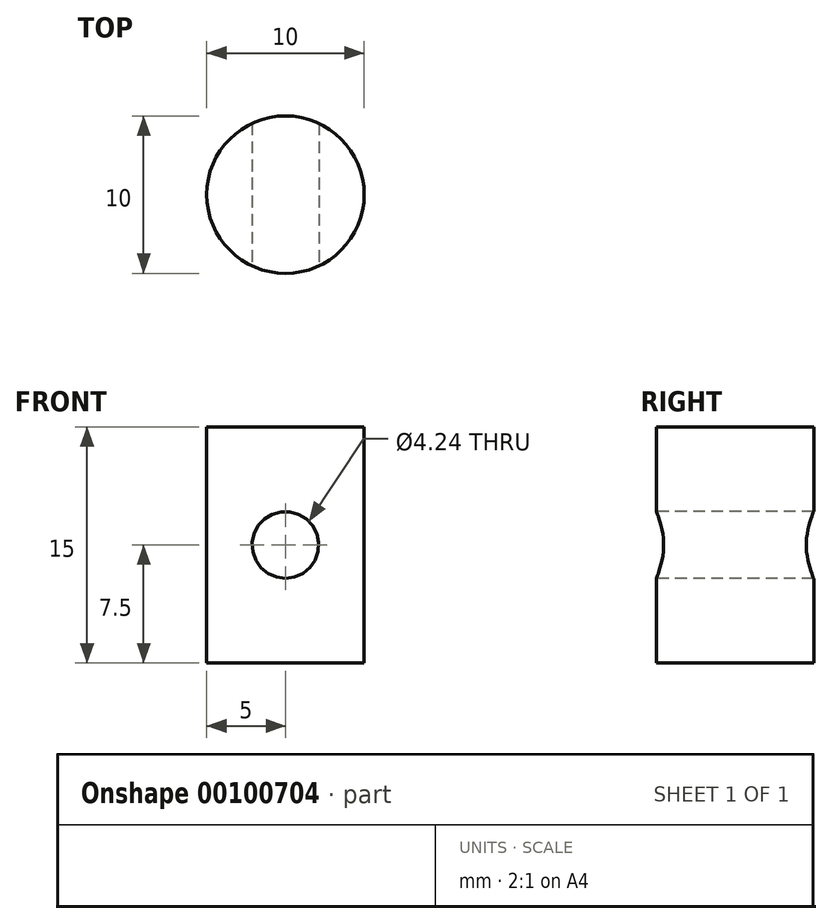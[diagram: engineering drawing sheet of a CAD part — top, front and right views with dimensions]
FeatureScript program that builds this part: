
annotation { "Feature Type Name" : "Feature", "Feature Type Description" : "" }
export const myFeature = defineFeature(function(context is Context, id is Id, definition is map)
    precondition{}
    {
        {
            var Q0;
            Q0=qCreatedBy(makeId("Top.planeOp"),FACE);
            var sketch = newSketch(context, id + "F0", { "sketchPlane" : qUnion([Q0])});
            skCircle(sketch, "E0", {"center": v(0, 0) * mm, "radius": 5 * mm});
            skSolve(sketch);
        }
        {
            var Q0;
            Q0 = qSketchRegion(id + "F0", true);
            extrude(context, id + "F1", {"entities" : qUnion([Q0]), "depth" : 15 * mm, "symmetric" : true});
        }
        {
            var Q0;
            Q0=qCreatedBy(makeId("Front.planeOp"),FACE);
            cPlane(context, id + "F2", {"entities" : qUnion([Q0]), "cplaneType" : CPlaneType.OFFSET, "offset" : 25 * mm, "width" : 150 * mm, "height" : 150 * mm});
        }
        {
            var Q0;
            Q0=qCreatedBy(id+"F2.planeOp",FACE);
            var sketch = newSketch(context, id + "F4", { "sketchPlane" : qUnion([Q0])});
            skCircle(sketch, "E1", {"center": v(0, 0) * mm, "radius": 2.12 * mm});
            skSolve(sketch);
        }
        {
            var Q0;
            Q0 = qSketchRegion(id + "F4", true);
            extrude(context, id + "F3", {"entities" : qUnion([Q0]), "operationType" : NewBodyOperationType.REMOVE, "endBound" : BoundingType.THROUGH_ALL, "oppositeDirection" : true, "depth" : 25 * mm});
        }
    });
